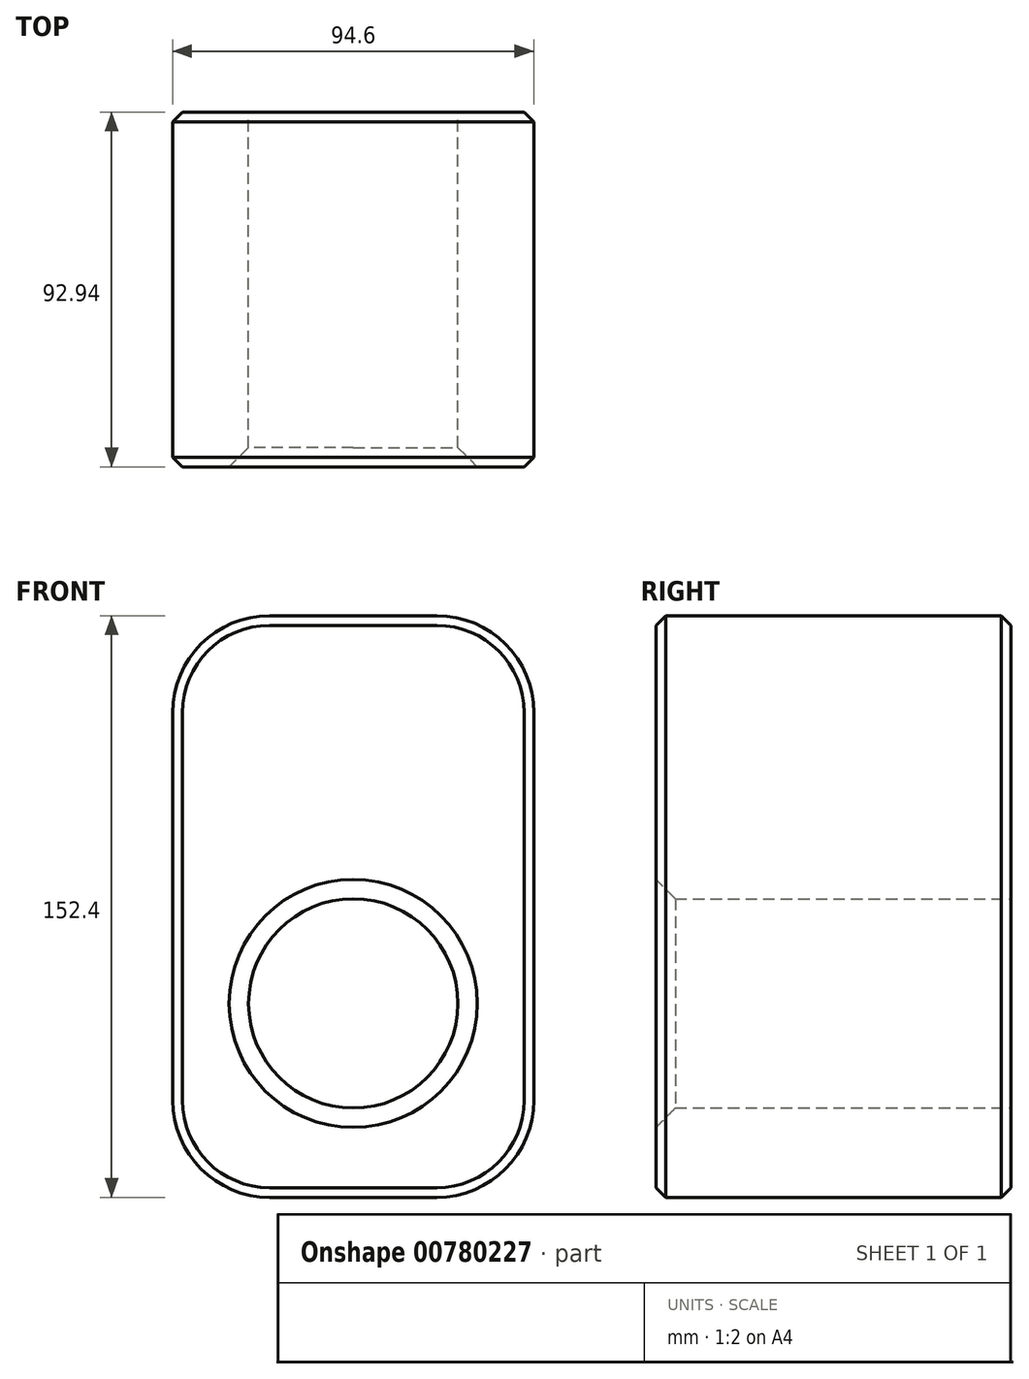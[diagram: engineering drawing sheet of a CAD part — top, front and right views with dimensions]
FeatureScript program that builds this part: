
annotation { "Feature Type Name" : "Feature", "Feature Type Description" : "" }
export const myFeature = defineFeature(function(context is Context, id is Id, definition is map)
    precondition{}
    {
        {
            var Q0;
            Q0=qCreatedBy(makeId("Top.planeOp"),FACE);
            var sketch = newSketch(context, id + "F0", { "sketchPlane" : qUnion([Q0])});
            skLineSegment(sketch, "E0.bottom", {"start": v(47.3, -46.47) * mm, "end": v(-47.3, -46.47) * mm});
            skLineSegment(sketch, "E0.top", {"start": v(47.3, 46.47) * mm, "end": v(-47.3, 46.47) * mm});
            skLineSegment(sketch, "E0.left", {"start": v(47.3, -46.47) * mm, "end": v(47.3, 46.47) * mm});
            skLineSegment(sketch, "E0.right", {"start": v(-47.3, -46.47) * mm, "end": v(-47.3, 46.47) * mm});
            skPoint(sketch, "E0.middle", {"position": v(0, 0) * mm});
            skSolve(sketch);
        }
        {
            var Q0;
            Q0=makeQuery(id+"F0.imprint","IMPRINT",FACE,{"disambiguationData":[TD([[makeQuery(id+"F0.imprint","IMPRINT",EDGE,{"derivedFrom":sQuery(id+"F0.wireOp",EDGE,"E0.bottom")}),-1.0]])]});
            extrude(context, id + "F1", {"entities" : qUnion([Q0]), "depth" : 101.6 * mm, "offsetDistance" : 25.4 * mm, "hasSecondDirection" : true, "secondDirectionOppositeDirection" : true, "secondDirectionDepth" : 50.8 * mm});
        }
        {
            var Q0;
            Q0=makeQuery(id+"F1.opExtrude","CAP_EDGE",EDGE,{"disambiguationData":[OSD([sQuery(id+"F0.wireOp",EDGE,"E0.right")])],"isStart":false});
            var Q1;
            Q1=makeQuery(id+"F1.opExtrude","CAP_EDGE",EDGE,{"disambiguationData":[OSD([sQuery(id+"F0.wireOp",EDGE,"E0.left")])],"isStart":false});
            var Q2;
            Q2=makeQuery(id+"F1.opExtrude","CAP_EDGE",EDGE,{"disambiguationData":[OSD([sQuery(id+"F0.wireOp",EDGE,"E0.right")])],"isStart":true});
            var Q3;
            Q3=makeQuery(id+"F1.opExtrude","CAP_EDGE",EDGE,{"disambiguationData":[OSD([sQuery(id+"F0.wireOp",EDGE,"E0.left")])],"isStart":true});
            fillet(context, id + "F2", {"entities" : qUnion([Q0, Q1, Q2, Q3]), "radius" : 25.4 * mm, "tangentPropagation" : true, "allowEdgeOverflow" : false});
        }
        {
            var Q0;
            Q0=makeQuery(id+"F1.opExtrude","SWEPT_EDGE",EDGE,{"disambiguationData":[OSD([sQuery(id+"F0.wireOp",EDGE,"E0.top"),sQuery(id+"F0.wireOp",EDGE,"E0.left")])]});
            var Q1;
            Q1=makeQuery(id+"F1.opExtrude","SWEPT_EDGE",EDGE,{"disambiguationData":[OSD([sQuery(id+"F0.wireOp",EDGE,"E0.bottom"),sQuery(id+"F0.wireOp",EDGE,"E0.left")])]});
            chamfer(context, id + "F3", {"entities" : qUnion([Q0, Q1]), "width" : 2.54 * mm, "tangentPropagation" : true});
        }
        {
            var Q0;
            Q0=makeQuery(id+"F1.opExtrude","SWEPT_FACE",FACE,{"disambiguationData":[OSD([sQuery(id+"F0.wireOp",EDGE,"E0.top")])]});
            var sketch = newSketch(context, id + "F4", { "sketchPlane" : qUnion([Q0])});
            skCircle(sketch, "E1", {"center": v(0, 0) * mm, "radius": 27.41 * mm});
            skSolve(sketch);
        }
        {
            var Q0;
            Q0=makeQuery(id+"F4.imprint","IMPRINT",FACE,{"disambiguationData":[TD([[makeQuery(id+"F4.imprint","IMPRINT",EDGE,{"derivedFrom":sQuery(id+"F4.wireOp",EDGE,"E1")}),1.0]])]});
            extrude(context, id + "F5", {"entities" : qUnion([Q0]), "operationType" : NewBodyOperationType.REMOVE, "oppositeDirection" : true, "depth" : 138.79 * mm, "offsetDistance" : 25.4 * mm});
        }
        {
            var Q0;
            Q0=makeQuery(id+"F5.boolean.opBoolean","INTERSECT",EDGE,{"derivedFrom":[makeQuery(id+"F1.opExtrude","SWEPT_FACE",FACE,{"disambiguationData":[OSD([sQuery(id+"F0.wireOp",EDGE,"E0.bottom")])]}),makeQuery(id+"F5.opExtrude","SWEPT_FACE",FACE,{"disambiguationData":[OSD([sQuery(id+"F4.wireOp",EDGE,"E1")])]})]});
            var Q1;
            Q1=makeQuery(id+"F5.boolean.opBoolean","COPY",EDGE,{"derivedFrom":makeQuery(id+"F5.opExtrude","CAP_EDGE",EDGE,{"disambiguationData":[OSD([sQuery(id+"F4.wireOp",EDGE,"E1")])],"isStart":true})});
            chamfer(context, id + "F6", {"entities" : qUnion([Q0, Q1]), "width" : 5.08 * mm, "tangentPropagation" : true});
        }
    });
